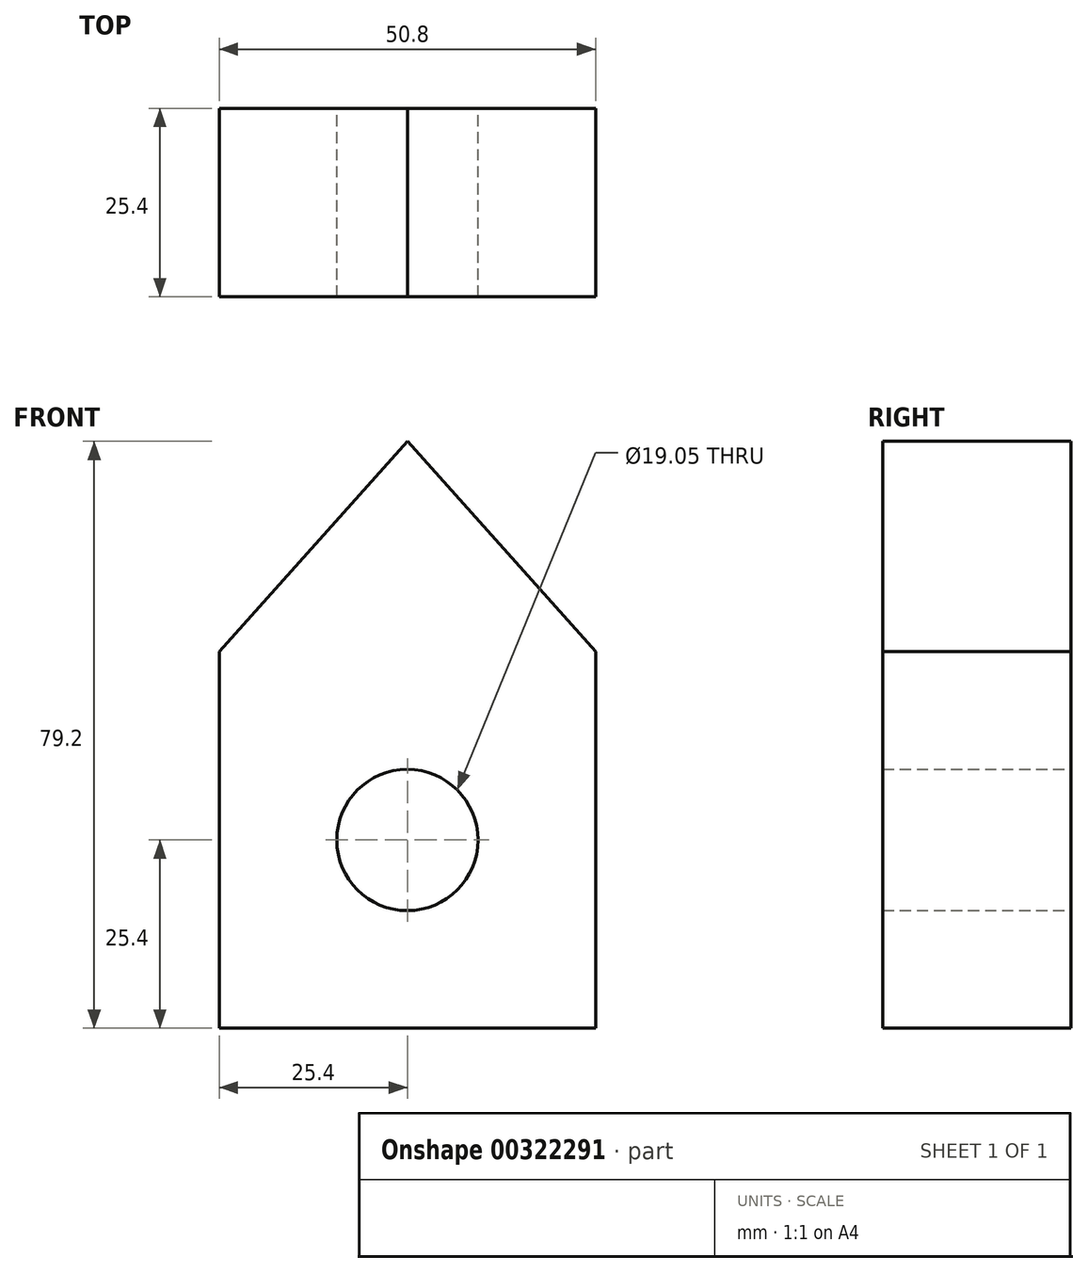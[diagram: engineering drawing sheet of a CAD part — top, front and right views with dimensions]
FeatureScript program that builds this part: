
annotation { "Feature Type Name" : "Feature", "Feature Type Description" : "" }
export const myFeature = defineFeature(function(context is Context, id is Id, definition is map)
    precondition{}
    {
        {
            var Q0;
            Q0=qCreatedBy(makeId("Front.planeOp"),FACE);
            var sketch = newSketch(context, id + "F0", { "sketchPlane" : qUnion([Q0])});
            skLineSegment(sketch, "E0.bottom", {"start": v(-25.4, -25.4) * mm, "end": v(25.4, -25.4) * mm});
            skLineSegment(sketch, "E0.top", {"start": v(-25.4, 25.4) * mm, "end": v(25.4, 25.4) * mm});
            skLineSegment(sketch, "E0.left", {"start": v(-25.4, -25.4) * mm, "end": v(-25.4, 25.4) * mm});
            skLineSegment(sketch, "E0.right", {"start": v(25.4, -25.4) * mm, "end": v(25.4, 25.4) * mm});
            skPoint(sketch, "E0.middle", {"position": v(0, 0) * mm});
            skLineSegment(sketch, "E1", {"start": v(-25.4, 25.4) * mm, "end": v(0, 53.8) * mm});
            skLineSegment(sketch, "E2", {"start": v(25.4, 25.4) * mm, "end": v(0, 53.8) * mm});
            skCircle(sketch, "E3", {"center": v(0, 0) * mm, "radius": 9.53 * mm});
            skSolve(sketch);
        }
        {
            var Q0;
            Q0 = qSketchRegion(id + "F0", true);
            extrude(context, id + "F1", {"entities" : qUnion([Q0]), "depth" : 25.4 * mm});
        }
    });
